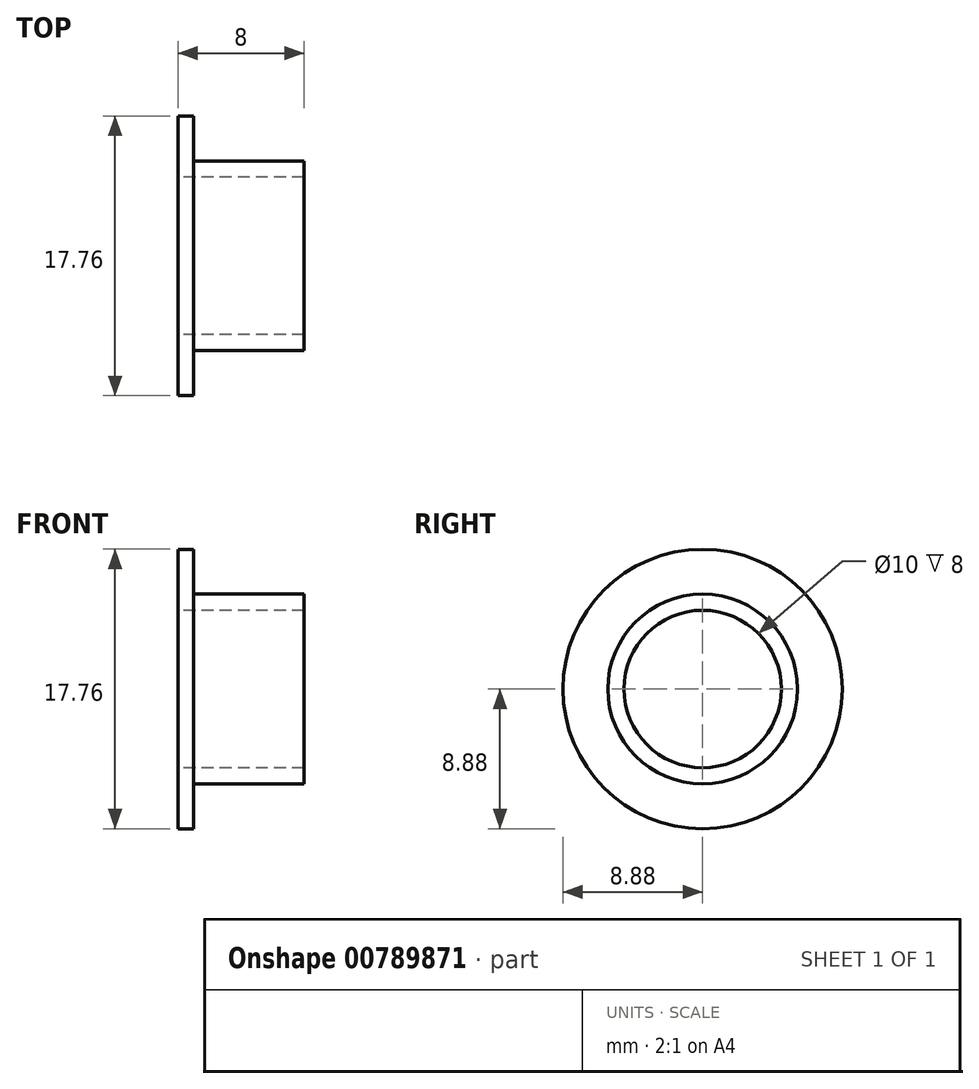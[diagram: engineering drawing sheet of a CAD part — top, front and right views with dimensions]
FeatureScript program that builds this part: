
annotation { "Feature Type Name" : "Feature", "Feature Type Description" : "" }
export const myFeature = defineFeature(function(context is Context, id is Id, definition is map)
    precondition{}
    {
        {
            var Q0;
            Q0=qCreatedBy(makeId("Front.planeOp"),FACE);
            var sketch = newSketch(context, id + "F0", { "sketchPlane" : qUnion([Q0])});
            skLineSegment(sketch, "E0", {"start": v(0, 0) * mm, "end": v(9.82, 0) * mm, "construction": true});
            skLineSegment(sketch, "E1", {"start": v(0, 5) * mm, "end": v(8, 5) * mm});
            skLineSegment(sketch, "E2", {"start": v(8, 5) * mm, "end": v(8, 6.03) * mm});
            skLineSegment(sketch, "E3", {"start": v(8, 6.03) * mm, "end": v(1, 6.03) * mm});
            skLineSegment(sketch, "E4", {"start": v(1, 6.03) * mm, "end": v(1, 8.88) * mm});
            skLineSegment(sketch, "E5", {"start": v(1, 8.88) * mm, "end": v(0, 8.88) * mm});
            skLineSegment(sketch, "E6", {"start": v(0, 8.88) * mm, "end": v(0, 5) * mm});
            skSolve(sketch);
        }
        {
            var Q0;
            Q0 = qSketchRegion(id + "F0", true);
            var Q1;
            Q1=sQuery(id+"F0.wireOp",EDGE,"E0");
            revolve(context, id + "F1", {"surfaceOperationType" : NewSurfaceOperationType.NEW, "entities" : qUnion([Q0]), "axis" : qUnion([Q1]), "revolveType" : RevolveType.FULL});
        }
    });
